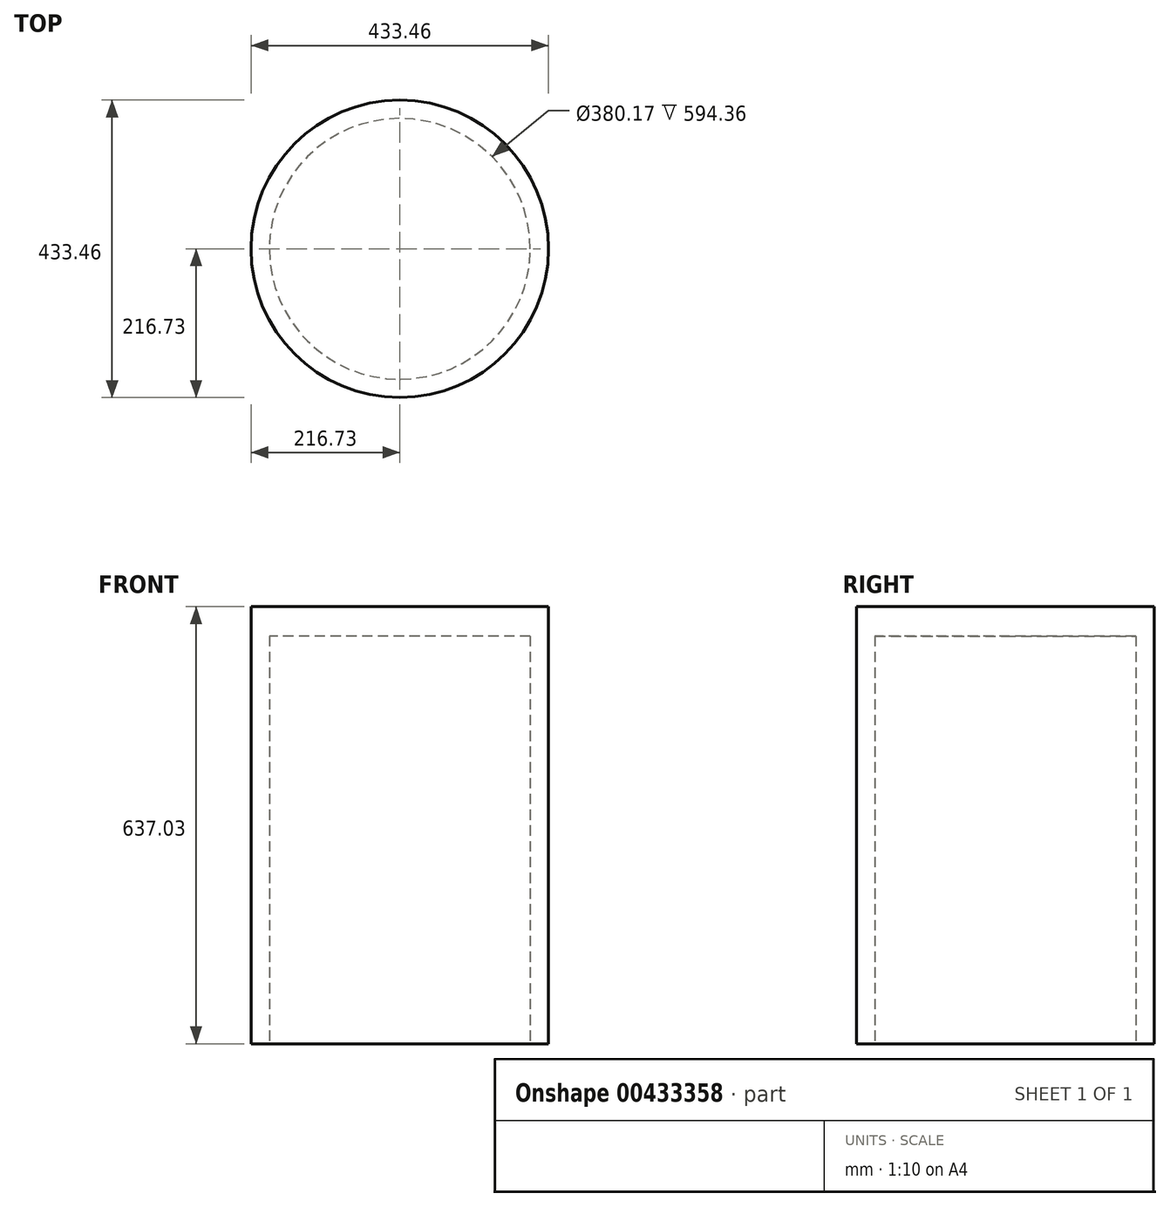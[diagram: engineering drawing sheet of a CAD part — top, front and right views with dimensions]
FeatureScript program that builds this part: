
annotation { "Feature Type Name" : "Feature", "Feature Type Description" : "" }
export const myFeature = defineFeature(function(context is Context, id is Id, definition is map)
    precondition{}
    {
        {
            var Q0;
            Q0=qCreatedBy(makeId("Top.planeOp"),FACE);
            var sketch = newSketch(context, id + "F0", { "sketchPlane" : qUnion([Q0])});
            skCircle(sketch, "E0", {"center": v(0, 0) * mm, "radius": 216.73 * mm});
            skSolve(sketch);
        }
        {
            var Q0;
            Q0=makeQuery(id+"F0.imprint","IMPRINT",FACE,{"disambiguationData":[TD([[makeQuery(id+"F0.imprint","IMPRINT",EDGE,{"derivedFrom":sQuery(id+"F0.wireOp",EDGE,"E0")}),1.0]])]});
            extrude(context, id + "F1", {"entities" : qUnion([Q0]), "depth" : 116.33 * mm});
        }
        {
            var Q0;
            Q0=qCreatedBy(makeId("Top.planeOp"),FACE);
            var sketch = newSketch(context, id + "F2", { "sketchPlane" : qUnion([Q0])});
            skCircle(sketch, "E1", {"center": v(0, 0) * mm, "radius": 190.09 * mm});
            skSolve(sketch);
        }
        {
            var Q0;
            Q0=makeQuery(id+"F1.opExtrude","CAP_FACE",FACE,{"disambiguationData":[OSD([sQuery(id+"F0.wireOp",EDGE,"E0")])],"isStart":false});
            extrude(context, id + "F3", {"entities" : qUnion([Q0]), "operationType" : NewBodyOperationType.ADD, "depth" : 520.7 * mm});
        }
        {
            var Q0;
            Q0=makeQuery(id+"F2.imprint","IMPRINT",FACE,{"disambiguationData":[TD([[makeQuery(id+"F2.imprint","IMPRINT",EDGE,{"derivedFrom":sQuery(id+"F2.wireOp",EDGE,"E1")}),1.0]])]});
            extrude(context, id + "F4", {"entities" : qUnion([Q0]), "operationType" : NewBodyOperationType.REMOVE, "depth" : 594.36 * mm});
        }
    });
